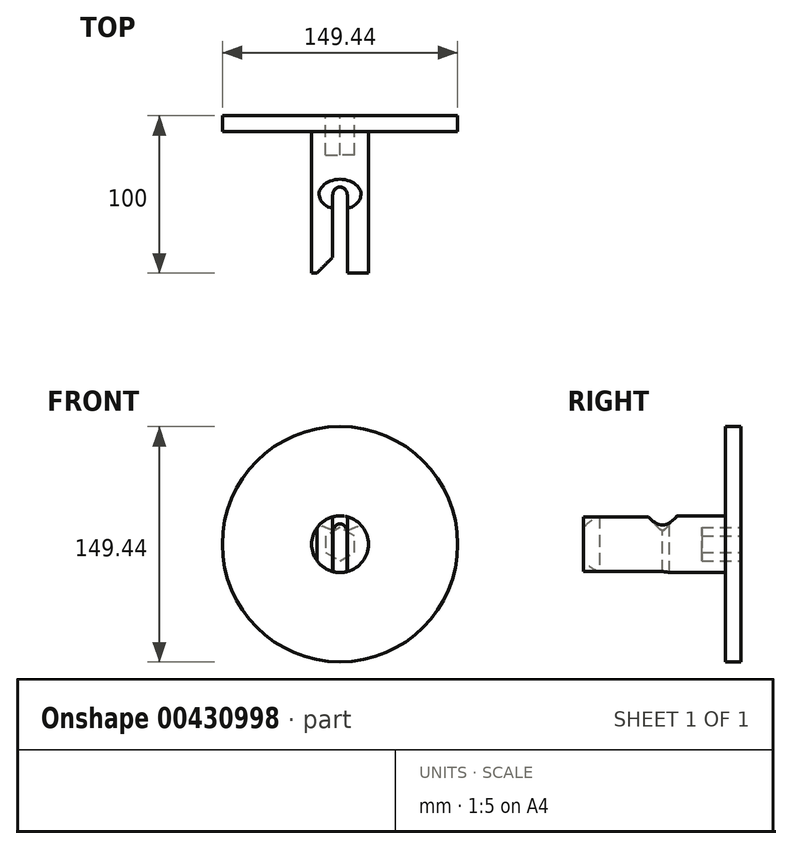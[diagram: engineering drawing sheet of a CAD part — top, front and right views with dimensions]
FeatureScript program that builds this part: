
annotation { "Feature Type Name" : "Feature", "Feature Type Description" : "" }
export const myFeature = defineFeature(function(context is Context, id is Id, definition is map)
    precondition{}
    {
        {
            var Q0;
            Q0=qCreatedBy(makeId("Front.planeOp"),FACE);
            var sketch = newSketch(context, id + "F0", { "sketchPlane" : qUnion([Q0])});
            skCircle(sketch, "E0", {"center": v(0, 0) * mm, "radius": 18.02 * mm});
            skSolve(sketch);
        }
        {
            var Q0;
            Q0=makeQuery(id+"F0.imprint","IMPRINT",FACE,{"disambiguationData":[TD([[makeQuery(id+"F0.imprint","IMPRINT",EDGE,{"derivedFrom":sQuery(id+"F0.wireOp",EDGE,"E0")}),1.0]])]});
            extrude(context, id + "F1", {"entities" : qUnion([Q0]), "endBound" : BoundingType.SYMMETRIC, "depth" : 100 * mm});
        }
        {
            var Q0;
            Q0=makeQuery(id+"F1.opExtrude","CAP_FACE",FACE,{"disambiguationData":[OSD([sQuery(id+"F0.wireOp",EDGE,"E0")])],"isStart":false});
            var sketch = newSketch(context, id + "F2", { "sketchPlane" : qUnion([Q0])});
            skLineSegment(sketch, "E1.bottom", {"start": v(4.74, -107.28) * mm, "end": v(-4.74, -107.28) * mm});
            skLineSegment(sketch, "E1.top", {"start": v(4.74, 107.28) * mm, "end": v(-4.74, 107.28) * mm});
            skLineSegment(sketch, "E1.left", {"start": v(4.74, -107.28) * mm, "end": v(4.74, 107.28) * mm});
            skLineSegment(sketch, "E1.right", {"start": v(-4.74, -107.28) * mm, "end": v(-4.74, 107.28) * mm});
            skPoint(sketch, "E1.middle", {"position": v(0, 0) * mm});
            skSolve(sketch);
        }
        {
            var Q0;
            Q0=qCreatedBy(makeId("Top.planeOp"),FACE);
            var sketch = newSketch(context, id + "F3", { "sketchPlane" : qUnion([Q0])});
            skCircle(sketch, "E2", {"center": v(0, 0) * mm, "radius": 4.6 * mm});
            skSolve(sketch);
        }
        {
            var Q0;
            Q0=makeQuery(id+"F1.opExtrude","CAP_FACE",FACE,{"disambiguationData":[OSD([sQuery(id+"F0.wireOp",EDGE,"E0")])],"isStart":true});
            var sketch = newSketch(context, id + "F4", { "sketchPlane" : qUnion([Q0])});
            skCircle(sketch, "E3", {"center": v(0, 0) * mm, "radius": 74.72 * mm});
            skSolve(sketch);
        }
        {
            var Q0;
            Q0 = qSketchRegion(id + "F4", true);
            extrude(context, id + "F5", {"entities" : qUnion([Q0]), "operationType" : NewBodyOperationType.ADD, "oppositeDirection" : true, "depth" : 10 * mm});
        }
        {
            var Q0;
            Q0 = qSketchRegion(id + "F2", true);
            extrude(context, id + "F6", {"entities" : qUnion([Q0]), "operationType" : NewBodyOperationType.REMOVE, "oppositeDirection" : true, "depth" : 50 * mm});
        }
        {
            var Q0;
            Q0 = qSketchRegion(id + "F3", true);
            extrude(context, id + "F7", {"entities" : qUnion([Q0]), "operationType" : NewBodyOperationType.REMOVE, "endBound" : BoundingType.SYMMETRIC, "oppositeDirection" : true, "depth" : 225 * mm});
        }
        {
            var Q0;
            Q0=makeQuery(id+"F7.boolean.opBoolean","INTERSECT",EDGE,{"disambiguationData":[OD(1.0)],"derivedFrom":[makeQuery(id+"F1.opExtrude","SWEPT_FACE",FACE,{"disambiguationData":[OSD([sQuery(id+"F0.wireOp",EDGE,"E0")])]}),makeQuery(id+"F7.opExtrude","SWEPT_FACE",FACE,{"disambiguationData":[OSD([sQuery(id+"F3.wireOp",EDGE,"E2")])]})]});
            chamfer(context, id + "F8", {"entities" : qUnion([Q0]), "width" : 5 * mm, "tangentPropagation" : true});
        }
        {
            var Q0;
            Q0=makeQuery(id+"F6.boolean.opBoolean","COPY",EDGE,{"derivedFrom":makeQuery(id+"F6.opExtrude","CAP_EDGE",EDGE,{"disambiguationData":[OSD([sQuery(id+"F2.wireOp",EDGE,"E1.left")])],"isStart":true})});
            var Q1;
            Q1=makeQuery(id+"F6.boolean.opBoolean","COPY",EDGE,{"derivedFrom":makeQuery(id+"F6.opExtrude","CAP_EDGE",EDGE,{"disambiguationData":[OSD([sQuery(id+"F2.wireOp",EDGE,"E1.right")])],"isStart":true})});
            chamfer(context, id + "F9", {"entities" : qUnion([Q0, Q1]), "width" : 10 * mm, "tangentPropagation" : true});
        }
        {
            var Q0;
            Q0=makeQuery(id+"F5.boolean.opBoolean","MERGE",FACE,{"derivedFrom":[makeQuery(id+"F1.opExtrude","CAP_FACE",FACE,{"disambiguationData":[OSD([sQuery(id+"F0.wireOp",EDGE,"E0")])],"isStart":true}),makeQuery(id+"F5.opExtrude","CAP_FACE",FACE,{"disambiguationData":[OSD([sQuery(id+"F4.wireOp",EDGE,"E3")])],"isStart":true})]});
            var sketch = newSketch(context, id + "F10", { "sketchPlane" : qUnion([Q0])});
            skCircle(sketch, "E4.cCircle", {"center": v(0, 0) * mm, "radius": 10.57 * mm, "construction": true});
            skLineSegment(sketch, "E4.0", {"start": v(9.15, -5.28) * mm, "end": v(0, -10.57) * mm});
            skLineSegment(sketch, "E4.1", {"start": v(0, -10.57) * mm, "end": v(-9.15, -5.28) * mm});
            skLineSegment(sketch, "E4.2", {"start": v(-9.15, -5.28) * mm, "end": v(-9.15, 5.28) * mm});
            skLineSegment(sketch, "E4.3", {"start": v(-9.15, 5.28) * mm, "end": v(0, 10.57) * mm});
            skLineSegment(sketch, "E4.4", {"start": v(0, 10.57) * mm, "end": v(9.15, 5.28) * mm});
            skLineSegment(sketch, "E4.5", {"start": v(9.15, 5.28) * mm, "end": v(9.15, -5.28) * mm});
            skSolve(sketch);
        }
        {
            var Q0;
            Q0=makeQuery(id+"F10.imprint","IMPRINT",FACE,{"disambiguationData":[TD([[makeQuery(id+"F10.imprint","IMPRINT",EDGE,{"derivedFrom":sQuery(id+"F10.wireOp",EDGE,"E4.0")}),-1.0]])]});
            extrude(context, id + "F11", {"entities" : qUnion([Q0]), "operationType" : NewBodyOperationType.REMOVE, "oppositeDirection" : true, "depth" : 25 * mm});
        }
    });
